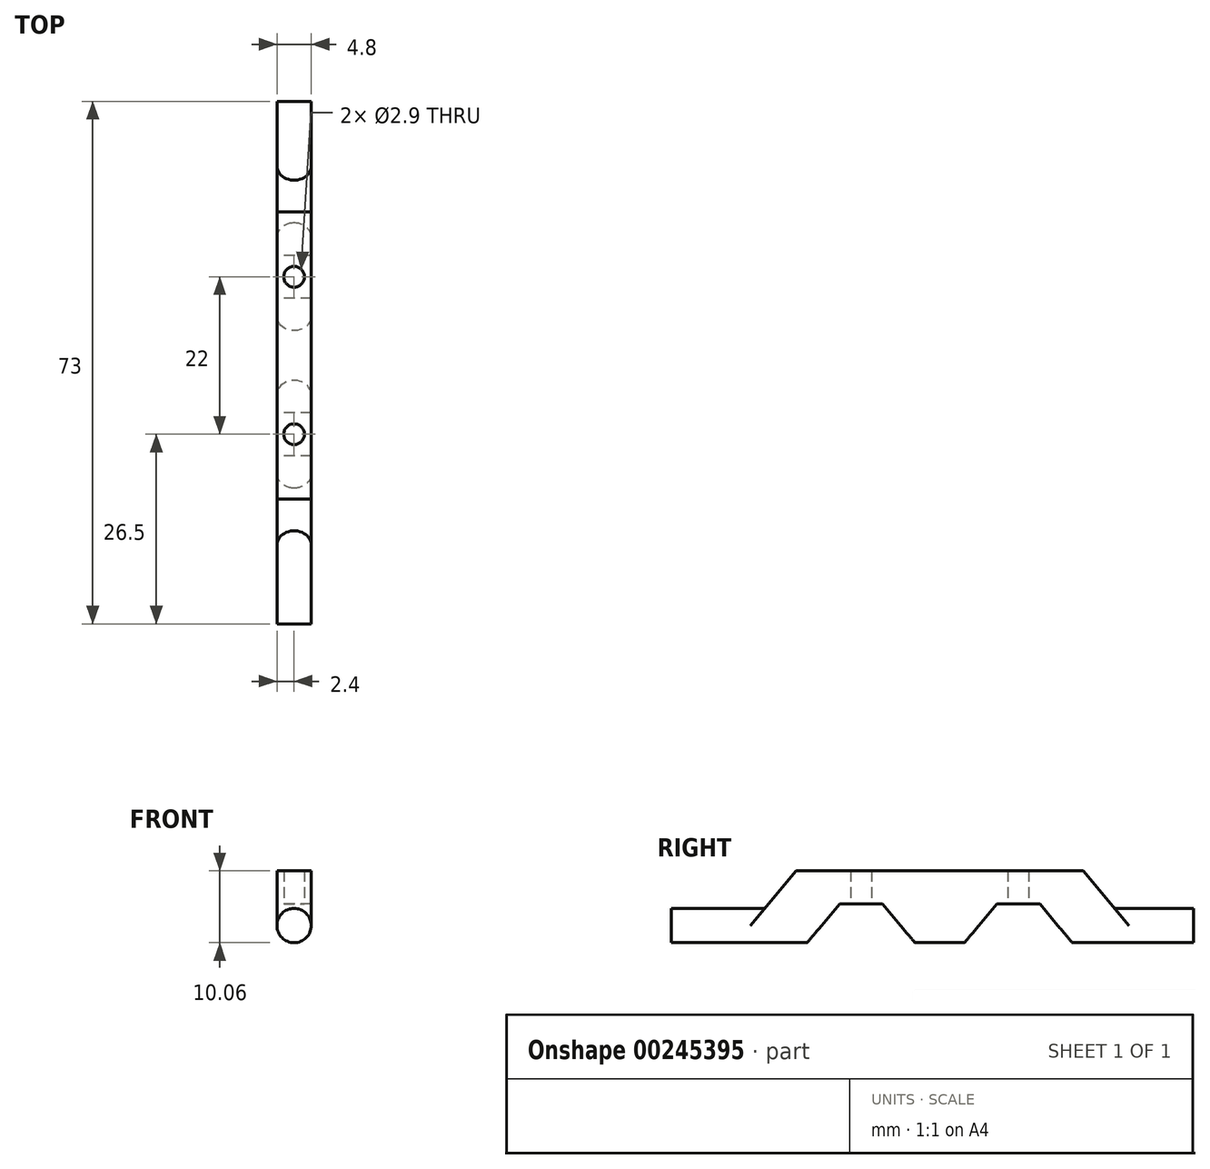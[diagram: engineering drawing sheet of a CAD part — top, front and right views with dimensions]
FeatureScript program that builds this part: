
annotation { "Feature Type Name" : "Feature", "Feature Type Description" : "" }
export const myFeature = defineFeature(function(context is Context, id is Id, definition is map)
    precondition{}
    {
        {
            var Q0;
            Q0=qCreatedBy(makeId("Front.planeOp"),FACE);
            var sketch = newSketch(context, id + "F0", { "sketchPlane" : qUnion([Q0])});
            skCircle(sketch, "E0", {"center": v(0, 0) * mm, "radius": 2.5 * mm});
            skSolve(sketch);
        }
        {
            var Q0;
            Q0=qSketchRegion(id+"F0",true);
            extrude(context, id + "F1", {"entities" : qUnion([Q0]), "depth" : 85 * mm});
        }
        {
            var Q0;
            Q0=qCreatedBy(makeId("Right.planeOp"),FACE);
            var sketch = newSketch(context, id + "F2", { "sketchPlane" : qUnion([Q0])});
            skLineSegment(sketch, "E1", {"start": v(0, 0) * mm, "end": v(-16, 0) * mm});
            skLineSegment(sketch, "E2", {"start": v(-16, 0) * mm, "end": v(-85, 0) * mm});
            skLineSegment(sketch, "E3", {"start": v(-85, 0) * mm, "end": v(-69, 0) * mm});
            skLineSegment(sketch, "E4", {"start": v(-69, 0) * mm, "end": v(-62.57, 7.66) * mm});
            skLineSegment(sketch, "E5", {"start": v(-16, 0) * mm, "end": v(-22.43, 7.66) * mm});
            skLineSegment(sketch, "E6", {"start": v(-22.43, 7.66) * mm, "end": v(-62.57, 7.66) * mm});
            skSolve(sketch);
        }
        {
            var Q0;
            Q0=qSketchRegion(id+"F2",true);
            extrude(context, id + "F3", {"entities" : qUnion([Q0]), "operationType" : NewBodyOperationType.ADD, "endBound" : BoundingType.SYMMETRIC, "depth" : 5 * mm});
        }
        {
            var Q0;
            Q0=makeQuery(id+"F3.opExtrude","CAP_FACE",FACE,{"disambiguationData":[OSD([sQuery(id+"F2.wireOp",EDGE,"E2"),sQuery(id+"F2.wireOp",EDGE,"E4"),sQuery(id+"F2.wireOp",EDGE,"E5"),sQuery(id+"F2.wireOp",EDGE,"E6")])],"isStart":true});
            var sketch = newSketch(context, id + "F4", { "sketchPlane" : qUnion([Q0])});
            skLineSegment(sketch, "E7", {"start": v(42.5, 0) * mm, "end": v(42.5, 3) * mm});
            skLineSegment(sketch, "E8", {"start": v(53.5, 3) * mm, "end": v(56.5, 3) * mm});
            skLineSegment(sketch, "E9", {"start": v(56.5, 3) * mm, "end": v(62.83, -4.54) * mm});
            skLineSegment(sketch, "E10", {"start": v(53.5, 3) * mm, "end": v(53.5, 1.19) * mm});
            skLineSegment(sketch, "E11.MirrorCS", {"start": v(53.5, 3) * mm, "end": v(50.5, 3) * mm});
            skLineSegment(sketch, "E12.MirrorCS", {"start": v(50.5, 3) * mm, "end": v(44.17, -4.54) * mm});
            skLineSegment(sketch, "E13.MirrorCS", {"start": v(34.5, 3) * mm, "end": v(40.83, -4.54) * mm});
            skLineSegment(sketch, "E14.MirrorCS", {"start": v(31.5, 3) * mm, "end": v(34.5, 3) * mm});
            skLineSegment(sketch, "E15.MirrorCS", {"start": v(31.5, 3) * mm, "end": v(28.5, 3) * mm});
            skLineSegment(sketch, "E16.MirrorCS", {"start": v(28.5, 3) * mm, "end": v(22.17, -4.54) * mm});
            skLineSegment(sketch, "E17", {"start": v(62.83, -4.54) * mm, "end": v(44.17, -4.54) * mm});
            skLineSegment(sketch, "E18", {"start": v(40.83, -4.54) * mm, "end": v(22.17, -4.54) * mm});
            skSolve(sketch);
        }
        {
            var Q0;
            Q0=qSketchRegion(id+"F4",true);
            extrude(context, id + "F5", {"entities" : qUnion([Q0]), "operationType" : NewBodyOperationType.REMOVE, "oppositeDirection" : true, "depth" : 25 * mm});
        }
        {
            var Q0;
            Q0=makeQuery(id+"F5.boolean.opBoolean","COPY",FACE,{"derivedFrom":makeQuery(id+"F5.opExtrude","SWEPT_FACE",FACE,{"disambiguationData":[OSD([sQuery(id+"F4.wireOp",EDGE,"E8"),sQuery(id+"F4.wireOp",EDGE,"E11.MirrorCS")])]})});
            var sketch = newSketch(context, id + "F6", { "sketchPlane" : qUnion([Q0])});
            skLineSegment(sketch, "E19", {"start": v(0, 56.5) * mm, "end": v(0, 50.5) * mm});
            skCircle(sketch, "E20", {"center": v(0, 53.5) * mm, "radius": 1.45 * mm});
            skSolve(sketch);
        }
        {
            var Q0;
            Q0=makeQuery(id+"F3.opExtrude","CAP_FACE",FACE,{"disambiguationData":[OSD([sQuery(id+"F2.wireOp",EDGE,"E2"),sQuery(id+"F2.wireOp",EDGE,"E4"),sQuery(id+"F2.wireOp",EDGE,"E5"),sQuery(id+"F2.wireOp",EDGE,"E6")])],"isStart":true});
            var sketch = newSketch(context, id + "F7", { "sketchPlane" : qUnion([Q0])});
            skLineSegment(sketch, "E21", {"start": v(53.5, 3) * mm, "end": v(53.5, 7.5) * mm});
            skLineSegment(sketch, "E22", {"start": v(53.5, 7.5) * mm, "end": v(19.92, 7.5) * mm});
            skLineSegment(sketch, "E23", {"start": v(19.92, 7.5) * mm, "end": v(19.92, 10.39) * mm});
            skLineSegment(sketch, "E24", {"start": v(19.92, 10.39) * mm, "end": v(66.52, 10.39) * mm});
            skLineSegment(sketch, "E25", {"start": v(66.52, 10.39) * mm, "end": v(66.52, 7.5) * mm});
            skLineSegment(sketch, "E26", {"start": v(66.52, 7.5) * mm, "end": v(53.5, 7.5) * mm});
            skSolve(sketch);
        }
        {
            var Q0;
            {var subQ2=sQuery(id+"F7.wireOp",EDGE,"E23");Q0=makeQuery(id+"F7.imprint","IMPRINT",FACE,{"disambiguationData":[TD([[makeQuery(id+"F7.imprint","IMPRINT",EDGE,{"derivedFrom":subQ2}),-1.0]])]});}
            extrude(context, id + "F8", {"entities" : qUnion([Q0]), "operationType" : NewBodyOperationType.REMOVE, "oppositeDirection" : true, "depth" : 25 * mm});
        }
        {
            var Q0;
            Q0=qSketchRegion(id+"F6",true);
            extrude(context, id + "F9", {"entities" : qUnion([Q0]), "operationType" : NewBodyOperationType.REMOVE, "oppositeDirection" : true, "depth" : 25 * mm});
        }
        {
            var Q0;
            Q0=makeQuery(id+"F5.boolean.opBoolean","COPY",FACE,{"derivedFrom":makeQuery(id+"F5.opExtrude","SWEPT_FACE",FACE,{"disambiguationData":[OSD([sQuery(id+"F4.wireOp",EDGE,"E14.MirrorCS"),sQuery(id+"F4.wireOp",EDGE,"E15.MirrorCS")])]})});
            var sketch = newSketch(context, id + "F10", { "sketchPlane" : qUnion([Q0])});
            skLineSegment(sketch, "E27", {"start": v(0, 34.5) * mm, "end": v(0, 28.5) * mm});
            skCircle(sketch, "E28", {"center": v(0, 31.5) * mm, "radius": 1.45 * mm});
            skSolve(sketch);
        }
        {
            var Q0;
            Q0=qSketchRegion(id+"F10",true);
            extrude(context, id + "F11", {"entities" : qUnion([Q0]), "operationType" : NewBodyOperationType.REMOVE, "oppositeDirection" : true, "depth" : 25 * mm});
        }
        {
            var Q0;
            Q0=makeQuery(id+"F1.opExtrude","CAP_FACE",FACE,{"disambiguationData":[OSD([sQuery(id+"F0.wireOp",EDGE,"E0")])],"isStart":false});
            var sketch = newSketch(context, id + "F12", { "sketchPlane" : qUnion([Q0])});
            skLineSegment(sketch, "E29", {"start": v(0, 0) * mm, "end": v(0, -3.5) * mm});
            skCircle(sketch, "E30", {"center": v(0, 0) * mm, "radius": 23.75 * mm});
            skCircle(sketch, "E31", {"center": v(0, 0) * mm, "radius": 13.75 * mm});
            skLineSegment(sketch, "E32", {"start": v(0, -3.5) * mm, "end": v(23.5, -3.5) * mm});
            skCircle(sketch, "E33", {"center": v(0, 0) * mm, "radius": 16.75 * mm});
            skCircle(sketch, "E34", {"center": v(0, 0) * mm, "radius": 20.75 * mm});
            skLineSegment(sketch, "E35", {"start": v(0, 0) * mm, "end": v(2.5, 0) * mm});
            skLineSegment(sketch, "E36", {"start": v(2.5, 0) * mm, "end": v(2.5, 28) * mm});
            skLineSegment(sketch, "E37", {"start": v(0, 0) * mm, "end": v(0, -1.5) * mm});
            skLineSegment(sketch, "E38", {"start": v(0, -1.5) * mm, "end": v(23.7, -1.5) * mm});
            skSolve(sketch);
        }
        {
            var Q0;
            {var subQ4=sQuery(id+"F12.wireOp",EDGE,"E35");Q0=makeQuery(id+"F12.imprint","IMPRINT",FACE,{"disambiguationData":[TD([[makeQuery(id+"F12.imprint","IMPRINT",EDGE,{"derivedFrom":subQ4}),1.0]])]});}
            var sketch = newSketch(context, id + "F13", { "sketchPlane" : qUnion([Q0])});
            skArc(sketch, "E39", {"start": v(-2.4, 0) * mm, "mid": v(0, -2.4) * mm, "end": v(2.4, 0) * mm});
            skLineSegment(sketch, "E40", {"start": v(-2.4, 0) * mm, "end": v(-2.4, 9.77) * mm});
            skLineSegment(sketch, "E41", {"start": v(-2.4, 9.77) * mm, "end": v(-6.2, 9.77) * mm});
            skLineSegment(sketch, "E42", {"start": v(-6.2, 9.77) * mm, "end": v(-6.2, -5.76) * mm});
            skLineSegment(sketch, "E43", {"start": v(-6.2, -5.76) * mm, "end": v(5.57, -5.76) * mm});
            skLineSegment(sketch, "E44", {"start": v(5.57, -5.76) * mm, "end": v(5.57, 8.85) * mm});
            skLineSegment(sketch, "E45", {"start": v(2.4, 0) * mm, "end": v(2.4, 9.16) * mm});
            skLineSegment(sketch, "E46", {"start": v(2.4, 9.16) * mm, "end": v(5.57, 8.85) * mm});
            skSolve(sketch);
        }
        {
            var Q0;
            Q0=qSketchRegion(id+"F13",true);
            extrude(context, id + "F14", {"entities" : qUnion([Q0]), "operationType" : NewBodyOperationType.REMOVE, "oppositeDirection" : true, "depth" : 102 * mm});
        }
        {
            var Q0;
            {var subQ4=sQuery(id+"F12.wireOp",EDGE,"E35");Q0=makeQuery(id+"F12.imprint","IMPRINT",FACE,{"disambiguationData":[TD([[makeQuery(id+"F12.imprint","IMPRINT",EDGE,{"derivedFrom":subQ4}),1.0]])]});}
            var sketch = newSketch(context, id + "F15", { "sketchPlane" : qUnion([Q0])});
            skArc(sketch, "E47", {"start": v(2.4, 0) * mm, "mid": v(0, 2.4) * mm, "end": v(-2.4, 0) * mm});
            skLineSegment(sketch, "E48", {"start": v(2.4, 0) * mm, "end": v(4.83, 0) * mm});
            skLineSegment(sketch, "E49", {"start": v(4.83, 0) * mm, "end": v(4.18, 8.08) * mm});
            skLineSegment(sketch, "E50", {"start": v(4.18, 8.08) * mm, "end": v(-2.94, 8.08) * mm});
            skLineSegment(sketch, "E51", {"start": v(-2.94, 8.08) * mm, "end": v(-3.46, 0) * mm});
            skLineSegment(sketch, "E52", {"start": v(-3.46, 0) * mm, "end": v(-2.4, 0) * mm});
            skSolve(sketch);
        }
        {
            var Q0;
            Q0=qSketchRegion(id+"F15",true);
            var Q1;
            Q1=makeQuery(id+"F3.opExtrude","SWEPT_FACE",FACE,{"disambiguationData":[OSD([sQuery(id+"F2.wireOp",EDGE,"E4")])]});
            extrude(context, id + "F16", {"entities" : qUnion([Q0]), "operationType" : NewBodyOperationType.REMOVE, "endBound" : BoundingType.UP_TO_SURFACE, "oppositeDirection" : true, "endBoundEntityFace" : qUnion([Q1]), "depth" : 25 * mm});
        }
        {
            var Q0;
            Q0=makeQuery(id+"F1.opExtrude","CAP_FACE",FACE,{"disambiguationData":[OSD([sQuery(id+"F0.wireOp",EDGE,"E0")])],"isStart":true});
            var sketch = newSketch(context, id + "F17", { "sketchPlane" : qUnion([Q0])});
            skArc(sketch, "E53", {"start": v(2.4, 0) * mm, "mid": v(0, 2.4) * mm, "end": v(-2.4, 0) * mm});
            skLineSegment(sketch, "E54", {"start": v(3.9, 0) * mm, "end": v(4.32, 8.69) * mm});
            skLineSegment(sketch, "E55", {"start": v(4.32, 8.69) * mm, "end": v(-4.98, 8.37) * mm});
            skLineSegment(sketch, "E56", {"start": v(-4.98, 8.37) * mm, "end": v(-3.42, 0) * mm});
            skLineSegment(sketch, "E57", {"start": v(-3.42, 0) * mm, "end": v(-2.4, 0) * mm});
            skLineSegment(sketch, "E58", {"start": v(2.4, 0) * mm, "end": v(3.9, 0) * mm});
            skSolve(sketch);
        }
        {
            var Q0;
            Q0=qSketchRegion(id+"F17",true);
            var Q1;
            Q1=makeQuery(id+"F3.opExtrude","SWEPT_FACE",FACE,{"disambiguationData":[OSD([sQuery(id+"F2.wireOp",EDGE,"E5")])]});
            extrude(context, id + "F18", {"entities" : qUnion([Q0]), "operationType" : NewBodyOperationType.REMOVE, "endBound" : BoundingType.UP_TO_SURFACE, "oppositeDirection" : true, "endBoundEntityFace" : qUnion([Q1]), "depth" : 25 * mm});
        }
        {
            var Q0;
            Q0=makeQuery(id+"F14.boolean.opBoolean","COPY",FACE,{"derivedFrom":makeQuery(id+"F14.opExtrude","SWEPT_FACE",FACE,{"disambiguationData":[OSD([sQuery(id+"F13.wireOp",EDGE,"E45")])]})});
            var sketch = newSketch(context, id + "F19", { "sketchPlane" : qUnion([Q0])});
            skLineSegment(sketch, "E59.0", {"start": v(0, -2.4) * mm, "end": v(0, 2.4) * mm});
            skLineSegment(sketch, "E60.0", {"start": v(-85, -20.75) * mm, "end": v(-85, 20.75) * mm});
            skLineSegment(sketch, "E61", {"start": v(-85, 20.75) * mm, "end": v(-80, 20.75) * mm});
            skLineSegment(sketch, "E62", {"start": v(-80, 20.75) * mm, "end": v(-80, -20.75) * mm});
            skLineSegment(sketch, "E63", {"start": v(-80, -20.75) * mm, "end": v(-85, -20.75) * mm});
            skLineSegment(sketch, "E64", {"start": v(0, 2.4) * mm, "end": v(-7, 2.4) * mm});
            skLineSegment(sketch, "E65", {"start": v(-7, 2.4) * mm, "end": v(-7, -4.52) * mm});
            skLineSegment(sketch, "E66", {"start": v(-7, -4.52) * mm, "end": v(0, -4.52) * mm});
            skLineSegment(sketch, "E67", {"start": v(0, -4.52) * mm, "end": v(0, -2.4) * mm});
            skSolve(sketch);
        }
        {
            var Q0;
            Q0 = qSketchRegion(id + "F19", true);
            extrude(context, id + "F20", {"entities" : qUnion([Q0]), "operationType" : NewBodyOperationType.REMOVE, "oppositeDirection" : true, "depth" : 25 * mm, "offsetDistance" : 25 * mm});
        }
    });
